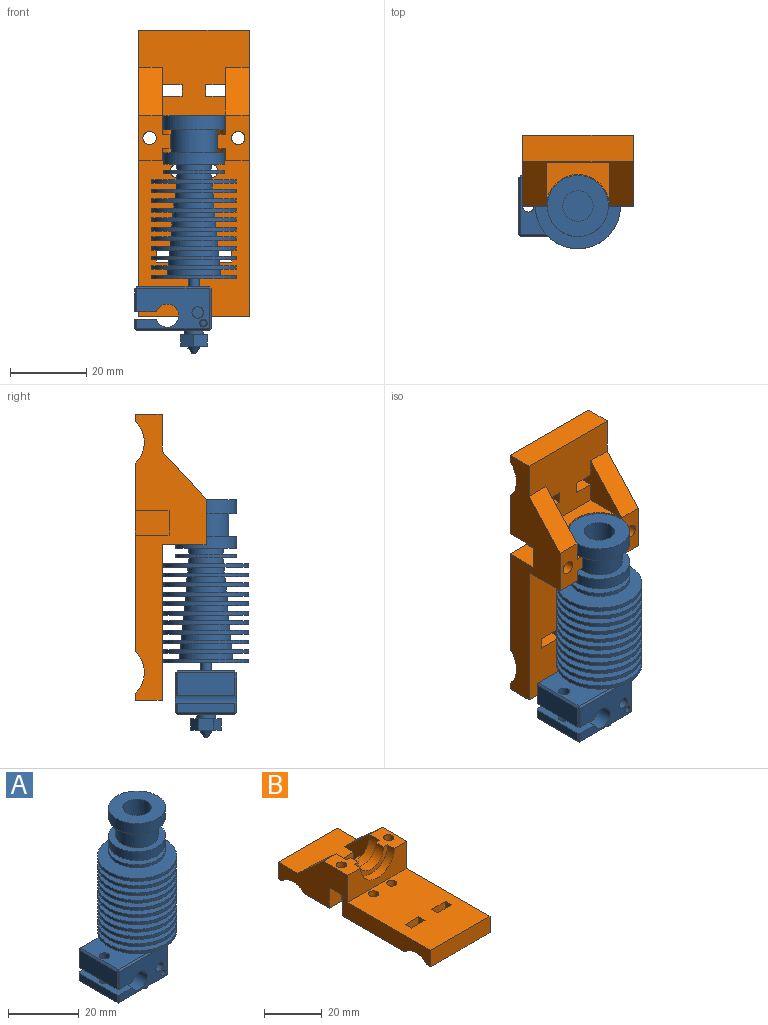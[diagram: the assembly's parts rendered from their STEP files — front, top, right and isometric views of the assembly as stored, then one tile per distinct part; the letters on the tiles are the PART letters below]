
ASSEMBLY  parts=2 mates=1
PART A: 111 faces, bbox 26.7x22.3x62.3 mm
  f0: plane 4.04x3mm, normal (-1,0,0), area 12.1mm2, adj f1,f2,f18,f62
  f1: plane 8.08x7mm, normal (0,0,-1), area 31.1mm2, adj f0,f2,f18,f60,f73,f87,f107
  f2: plane 3.5x3mm, normal (-0.5,0.87,0), area 12.1mm2, adj f0,f1,f62,f107
  f3: plane 0.5x0.5mm, normal (-0.58,0.58,0.58), area 0.2mm2, adj f83,f88,f89
  f4: plane 0.5x0.5mm, normal (0.58,0.58,0.58), area 0.2mm2, adj f65,f75,f88
  f5: plane 16x5.65mm, normal (0,0,-1), area 83mm2, adj f9,f63,f67,f89,f90,f92,f100
  f6: plane 19x15mm, normal (0,0,1), area 271.8mm2, adj f63,f65,f71,f81,f83,f88
  f7: plane 15x0.5mm, normal (-0.71,0,-0.71), area 10.6mm2, adj f20,f84,f95,f109
  f8: cylinder r=6mm len=12mm, axis (0,0,1), area 226.2mm2, adj f79,f110
  f9: plane 19x10.5mm, normal (0,1,0), area 160.7mm2, adj f5,f19,f66,f75,f88,f89,f92,f106
  f10: cylinder r=11.15mm len=22.3mm, axis (0,0,1), area 70.1mm2, adj f13,f14
  f11: plane 22.3x22.3mm, normal (0,0,-1), area 277.5mm2, adj f39,f40
  f12: cylinder r=11.15mm len=22.3mm, axis (0,0,1), area 70.1mm2, adj f21,f28
  f13: plane 22.3x22.3mm, normal (0,0,1), area 319.7mm2, adj f10,f74
  f14: plane 22.3x22.3mm, normal (0,0,-1), area 312mm2, adj f10,f27
  f15: plane 0.5x0.5mm, normal (0.58,0.58,-0.58), area 0.2mm2, adj f69,f75,f106
  f16: cylinder r=8mm len=16mm, axis (0,0,1), area 186mm2, adj f79,f103
  f17: plane 0.5x0.5mm, normal (-0.58,-0.58,0.58), area 0.2mm2, adj f71,f83,f90
  f18: plane 3.5x3mm, normal (-0.5,-0.87,0), area 12.1mm2, adj f0,f1,f62,f87
  f19: plane 2.5x0.5mm, normal (-0.71,0.71,0), area 1.8mm2, adj f9,f66,f95,f109
  f20: plane 19x15mm, normal (0,0,-1), area 258.3mm2, adj f7,f22,f61,f69,f106,f108
  f21: plane 22.3x22.3mm, normal (0,0,-1), area 304mm2, adj f12,f29
  f22: cylinder r=2.5mm len=5mm, axis (0,0,1), area 15.7mm2, adj f20,f62
  f23: plane 10.5x0.5mm, normal (0.71,-0.71,0), area 7.4mm2, adj f67,f82,f93,f97
  f24: cylinder r=8mm len=16mm, axis (0,0,1), area 50.3mm2, adj f25,f26
  f25: plane 16x16mm, normal (0,0,-1), area 137.4mm2, adj f24,f101
  f26: plane 16x16mm, normal (0,0,1), area 137.4mm2, adj f24,f99
  f27: cylinder r=5mm len=10mm, axis (0,0,1), area 47.1mm2, adj f14,f28
  f28: plane 22.3x22.3mm, normal (0,0,1), area 312mm2, adj f12,f27
  f29: cylinder r=5.25mm len=10.5mm, axis (0,0,1), area 49.5mm2, adj f21,f30
  f30: plane 22.3x22.3mm, normal (0,0,1), area 304mm2, adj f29,f31
  f31: cylinder r=11.15mm len=22.3mm, axis (0,0,1), area 70.1mm2, adj f30,f32
  f32: plane 22.3x22.3mm, normal (0,0,-1), area 295.5mm2, adj f31,f33
  f33: cylinder r=5.5mm len=11mm, axis (0,0,1), area 51.8mm2, adj f32,f34
  f34: plane 22.3x22.3mm, normal (0,0,1), area 295.5mm2, adj f33,f35
  f35: cylinder r=11.15mm len=22.3mm, axis (0,0,1), area 70.1mm2, adj f34,f36
  f36: plane 22.3x22.3mm, normal (0,0,-1), area 286.7mm2, adj f35,f37
  f37: cylinder r=5.75mm len=11.5mm, axis (0,0,1), area 54.2mm2, adj f36,f38
  f38: plane 22.3x22.3mm, normal (0,0,1), area 286.7mm2, adj f37,f39
  f39: cylinder r=11.15mm len=22.3mm, axis (0,0,1), area 70.1mm2, adj f11,f38
  f40: cylinder r=6mm len=12mm, axis (0,0,1), area 56.5mm2, adj f11,f41
  f41: plane 22.3x22.3mm, normal (0,0,1), area 277.5mm2, adj f40,f42
  f42: cylinder r=11.15mm len=22.3mm, axis (0,0,1), area 70.1mm2, adj f41,f43
  f43: plane 22.3x22.3mm, normal (0,0,-1), area 267.9mm2, adj f42,f44
  f44: cylinder r=6.25mm len=12.5mm, axis (0,0,1), area 58.9mm2, adj f43,f45
  f45: plane 22.3x22.3mm, normal (0,0,1), area 267.9mm2, adj f44,f46
  f46: cylinder r=11.15mm len=22.3mm, axis (0,0,1), area 70.1mm2, adj f45,f47
  f47: plane 22.3x22.3mm, normal (0,0,-1), area 257.8mm2, adj f46,f48
  f48: cylinder r=6.5mm len=13mm, axis (0,0,1), area 61.3mm2, adj f47,f49
  f49: plane 22.3x22.3mm, normal (0,0,1), area 257.8mm2, adj f48,f50
  f50: cylinder r=11.15mm len=22.3mm, axis (0,0,1), area 70.1mm2, adj f49,f51
  f51: plane 22.3x22.3mm, normal (0,0,-1), area 247.4mm2, adj f50,f52
  f52: cylinder r=6.75mm len=13.5mm, axis (0,0,1), area 63.6mm2, adj f51,f53
  f53: plane 22.3x22.3mm, normal (0,0,1), area 247.4mm2, adj f52,f54
  f54: cylinder r=11.15mm len=22.3mm, axis (0,0,1), area 70.1mm2, adj f53,f55
  f55: plane 22.3x22.3mm, normal (0,0,-1), area 236.6mm2, adj f54,f56
  f56: cylinder r=7mm len=14mm, axis (0,0,1), area 66mm2, adj f55,f57
  f57: plane 22.3x22.3mm, normal (0,0,1), area 236.6mm2, adj f56,f58
  f58: cylinder r=11.15mm len=22.3mm, axis (0,0,1), area 70.1mm2, adj f57,f59
  f59: plane 22.3x22.3mm, normal (0,0,-1), area 384.4mm2, adj f58,f81
  f60: plane 4.04x3mm, normal (1,0,0), area 12.1mm2, adj f1,f62,f87,f107
  f61: plane 19x0.5mm, normal (0,-0.71,-0.71), area 13.4mm2, adj f20,f67,f84,f93
  f62: plane 8.08x7mm, normal (0,0,1), area 22.8mm2, adj f0,f2,f18,f22,f60,f87,f107
  f63: cylinder r=1.5mm len=6.5mm, axis (0,0,1), area 61.3mm2, adj f5,f6
  f64: plane 0.4x0.4mm, normal (0,0,-1), area 0.1mm2, adj f94
  f65: plane 15x0.5mm, normal (0.71,0,0.71), area 10.6mm2, adj f4,f6,f82,f97
  f66: plane 16x5.65mm, normal (0,0,1), area 83mm2, adj f9,f19,f67,f91,f92,f108,f109
  f67: plane 19x10.5mm, normal (0,-1,0), area 150.5mm2, adj f5,f23,f61,f66,f71,f90,f91,f92
  f68: plane 8x8mm, normal (0,0,1), area 50.3mm2, adj f80
  f69: plane 15x0.5mm, normal (0.71,0,-0.71), area 10.6mm2, adj f15,f20,f82,f93
  f70: plane 1.55x1.55mm, normal (0,-1,0), area 1.9mm2, adj f98
  f71: plane 19x0.5mm, normal (0,-0.71,0.71), area 13.4mm2, adj f6,f17,f67,f97
  f72: plane 22.3x22.3mm, normal (0,0,1), area 327mm2, adj f77,f101
  f73: cone r=1.9mm half-angle=35deg, axis (0,0,1), area 18.4mm2, adj f1,f96
  f74: cylinder r=4.75mm len=9.5mm, axis (0,0,1), area 44.8mm2, adj f13,f102
  f75: plane 10.5x0.5mm, normal (0.71,0.71,0), area 7.4mm2, adj f4,f9,f15,f82
  f76: plane 16x16mm, normal (0,0,-1), area 137.4mm2, adj f78,f99
  f77: cylinder r=11.15mm len=22.3mm, axis (0,0,1), area 70.1mm2, adj f72,f102
  f78: cylinder r=8mm len=16mm, axis (0,0,1), area 150.8mm2, adj f76,f110
  f79: plane 16x16mm, normal (0,0,-1), area 88mm2, adj f8,f16
  f80: cylinder r=4mm len=8mm, axis (0,0,1), area 163.4mm2, adj f68,f103
  f81: cylinder r=1.4mm len=2.8mm, axis (0,0,1), area 18.5mm2, adj f6,f59
  f82: plane 15x10.5mm, normal (1,0,0), area 157.5mm2, adj f23,f65,f69,f75
  f83: plane 15x0.5mm, normal (-0.71,0,0.71), area 10.6mm2, adj f3,f6,f17,f100
  f84: plane 0.5x0.5mm, normal (-0.58,-0.58,-0.58), area 0.2mm2, adj f7,f61,f91
  f85: plane 2x2mm, normal (0,-1,0), area 1.3mm2, adj f98,f105
  f86: plane 3x3mm, normal (0,-1,0), area 7.1mm2, adj f104
  f87: plane 3.5x3mm, normal (0.5,-0.87,0), area 12.1mm2, adj f1,f18,f60,f62
  f88: plane 19x0.5mm, normal (0,0.71,0.71), area 13.4mm2, adj f3,f4,f6,f9
  f89: plane 6x0.5mm, normal (-0.71,0.71,0), area 4.2mm2, adj f3,f5,f9,f100
  f90: plane 6x0.5mm, normal (-0.71,-0.71,0), area 4.2mm2, adj f5,f17,f67,f100
  f91: plane 2.5x0.5mm, normal (-0.71,-0.71,0), area 1.8mm2, adj f66,f67,f84,f109
  f92: cylinder r=3.02mm len=16mm, axis (0,-1,0), area 271.5mm2, adj f5,f9,f66,f67
  f93: plane 0.5x0.5mm, normal (0.58,-0.58,-0.58), area 0.2mm2, adj f23,f61,f69
  f94: cylinder r=0.2mm len=3mm, axis (0,0,-1), area 3.8mm2, adj f64,f96
  f95: plane 0.5x0.5mm, normal (-0.58,0.58,-0.58), area 0.2mm2, adj f7,f19,f106
  f96: plane 1x1mm, normal (0,0,-1), area 0.7mm2, adj f73,f94
  f97: plane 0.5x0.5mm, normal (0.58,-0.58,0.58), area 0.2mm2, adj f23,f65,f71
  f98: cylinder r=0.78mm len=2.45mm, axis (0,-1,0), area 11.9mm2, adj f70,f85
  f99: cylinder r=4.5mm len=9mm, axis (0,0,1), area 42.4mm2, adj f26,f76
  f100: plane 15x6mm, normal (-1,0,0), area 90mm2, adj f5,f83,f89,f90
  f101: cylinder r=4.5mm len=9mm, axis (0,0,1), area 42.4mm2, adj f25,f72
  f102: plane 22.3x22.3mm, normal (0,0,-1), area 319.7mm2, adj f74,f77
  f103: plane 16x16mm, normal (0,0,1), area 150.8mm2, adj f16,f80
  f104: cylinder r=1.5mm len=3.45mm, axis (0,-1,0), area 32.5mm2, adj f67,f86
  f105: cylinder r=1mm len=2mm, axis (0,-1,0), area 12.6mm2, adj f67,f85
  f106: plane 19x0.5mm, normal (0,0.71,-0.71), area 13.4mm2, adj f9,f15,f20,f95
  f107: plane 3.5x3mm, normal (0.5,0.87,0), area 12.1mm2, adj f1,f2,f60,f62
  f108: cylinder r=1.5mm len=3mm, axis (0,0,1), area 28.3mm2, adj f20,f66
  f109: plane 15x2.5mm, normal (-1,0,0), area 37.5mm2, adj f7,f19,f66,f91
  f110: plane 16x16mm, normal (0,0,1), area 88mm2, adj f8,f78
PART B: 50 faces, bbox 29x75x18.5 mm
  f0: plane 12x8.25mm, normal (0,0,1), area 73mm2, adj f3,f10,f15,f16,f17,f18,f19,f20
  f1: plane 12x8.25mm, normal (0,0,1), area 73mm2, adj f2,f11,f15,f16,f17,f18,f19,f20
  f2: plane 74.96x18.5mm, normal (-1,0,0), area 642.2mm2, adj f1,f4,f6,f7,f12,f13,f14,f15
  f3: plane 74.96x18.5mm, normal (1,0,0), area 642.2mm2, adj f0,f4,f6,f7,f12,f13,f14,f15
  f4: plane 49.34x29mm, normal (0,0,-1), area 1259.9mm2, adj f2,f3,f7,f8,f9,f21,f22,f23
  f5: plane 16.5x11.5mm, normal (0,1,0), area 82.8mm2, adj f6,f17,f46,f47
  f6: plane 29x22.22mm, normal (0,0,1), area 456.4mm2, adj f2,f3,f5,f8,f9,f28,f29,f30
  f7: cylinder r=7.5mm len=29mm, axis (1,0,0), area 354.2mm2, adj f2,f3,f4,f12
  f8: plane 7x5.15mm, normal (0,-1,0), area 36mm2, adj f4,f6,f30,f46
  f9: plane 7x5.15mm, normal (0,1,0), area 36mm2, adj f4,f6,f30,f46
  f10: cylinder r=1.75mm len=9.7mm, axis (0,0,1), area 106.7mm2, adj f0,f42
  f11: cylinder r=1.75mm len=9.7mm, axis (0,0,1), area 106.7mm2, adj f1,f38
  f12: plane 29x1.9mm, normal (0,0,-1), area 55.1mm2, adj f2,f3,f7,f36
  f13: plane 40.74x29mm, normal (0,0,1), area 1121.4mm2, adj f2,f3,f15,f21,f22,f24,f25,f26
  f14: plane 29x1.9mm, normal (0,0,-1), area 55.1mm2, adj f2,f3,f23,f37
  f15: plane 29x11.5mm, normal (0,-1,0), area 226.6mm2, adj f0,f1,f2,f3,f13,f19
  f16: cylinder r=6.25mm len=12.5mm, axis (0,1,0), area 74.6mm2, adj f0,f1,f18,f20
  f17: cylinder r=8.25mm len=16.5mm, axis (0,1,0), area 129.6mm2, adj f0,f1,f5,f18
  f18: plane 16.5x8.25mm, normal (0,1,0), area 45.6mm2, adj f0,f1,f16,f17
  f19: cylinder r=8.25mm len=16.5mm, axis (0,-1,0), area 82.9mm2, adj f0,f1,f15,f20
  f20: plane 16.5x8.25mm, normal (0,-1,0), area 45.6mm2, adj f0,f1,f16,f19
  f21: cylinder r=1.75mm len=7mm, axis (0,0,-1), area 77mm2, adj f4,f13
  f22: cylinder r=1.75mm len=7mm, axis (0,0,-1), area 77mm2, adj f4,f13
  f23: cylinder r=7.5mm len=29mm, axis (1,0,0), area 354.2mm2, adj f2,f3,f4,f14
  f24: plane 7x3.01mm, normal (-1,0,0), area 21.1mm2, adj f4,f13,f25,f35
  f25: plane 7x6.76mm, normal (0,1,0), area 47.3mm2, adj f4,f13,f24,f32
  f26: plane 7x6.76mm, normal (0,1,0), area 47.3mm2, adj f4,f13,f27,f31
  f27: plane 7x3.01mm, normal (1,0,0), area 21.1mm2, adj f4,f13,f26,f34
  f28: plane 7x3.01mm, normal (1,0,0), area 21.1mm2, adj f4,f6,f29,f33
  f29: plane 7x5.15mm, normal (0,-1,0), area 36mm2, adj f4,f6,f28,f47
  f30: plane 7x3.01mm, normal (-1,0,0), area 21.1mm2, adj f4,f6,f8,f9
  f31: plane 7x3.01mm, normal (-1,0,0), area 21.1mm2, adj f4,f13,f26,f34
  f32: plane 7x3.01mm, normal (1,0,0), area 21.1mm2, adj f4,f13,f25,f35
  f33: plane 7x5.15mm, normal (0,1,0), area 36mm2, adj f4,f6,f28,f47
  f34: plane 7x6.76mm, normal (0,-1,0), area 47.3mm2, adj f4,f13,f27,f31
  f35: plane 7x6.76mm, normal (0,-1,0), area 47.3mm2, adj f4,f13,f24,f32
  f36: plane 29x7mm, normal (0,1,0), area 203mm2, adj f2,f3,f6,f12
  f37: plane 29x7mm, normal (0,-1,0), area 203mm2, adj f2,f3,f13,f14
  f38: plane 6.51x6.14mm, normal (0,0,-1), area 30.4mm2, adj f2,f11,f39,f40,f41
  f39: plane 8.8x6.14mm, normal (0,1,0), area 54.1mm2, adj f2,f4,f38,f41
  f40: plane 8.8x6.14mm, normal (0,-1,0), area 54.1mm2, adj f2,f4,f38,f41
  f41: plane 8.8x6.51mm, normal (-1,0,0), area 57.3mm2, adj f4,f38,f39,f40
  f42: plane 6.51x6.14mm, normal (0,0,-1), area 30.4mm2, adj f3,f10,f43,f44,f45
  f43: plane 8.8x6.14mm, normal (0,1,0), area 54.1mm2, adj f3,f4,f42,f44
  f44: plane 8.8x6.51mm, normal (1,0,0), area 57.3mm2, adj f4,f42,f43,f45
  f45: plane 8.8x6.14mm, normal (0,-1,0), area 54.1mm2, adj f3,f4,f42,f44
  f46: plane 18.5x12.57mm, normal (1,0,0), area 93.3mm2, adj f4,f5,f6,f8,f9,f49
  f47: plane 18.5x12.57mm, normal (-1,0,0), area 93.3mm2, adj f4,f5,f6,f29,f33,f48
  f48: plane 12.57x11.5mm, normal (0,0.68,0.74), area 106.5mm2, adj f0,f3,f6,f47
  f49: plane 12.57x11.5mm, normal (0,0.68,0.74), area 106.5mm2, adj f1,f2,f6,f46
PLACE A t=(-7.02,-10.97,8.4)mm
PLACE B rot(axis=(1,0,0),90deg) t=(-10.33,10.53,-4.67)mm
MATE fastened B.f16 <-> A.f8  axis (0,0,1) through (-10.02,-7.97,23.05)mm
